# Revit family: 6_天吊埋込タイプ 消音形 単相100V_3相200V-60
name_source: partatom
category: 機械設備
units: mm (PartAtom-declared; Revit-internal decimal feet)

## family parameters
OmniClass タイトル = Centrifugal Fans
OmniClass 番号 = 23.75.35.17.27
パーツ タイプ = 割り込み
ロード時にボイドで切り取り = いいえ
丸型コネクタ寸法 = 直径を使用
作業面ベース = いいえ
共有 = いいえ
常に垂直 = はい
部屋計算ポイント = はい

## types (18) — shared parameters
Clearance Left = 450  [stored 1.47638 ft]
IfcExportAs = IfcFanType
IfcExportType = CENTRIFUGALFORWARDCURVED
MID静圧 = 0.0 Pa
MID風量 = 0.0 m³/h
OmniClassCode = 23-33 31 19 13 15
URL = https://www.mitsubishielectric.co.jp
Uniclass2015Code = Pr_65_67_29_12
Uniclass2015Title = Centrifugal fans
Uniclass2015Version = Systems v1.9
サービススペース = はい
ファンの種類 = 多翼形
仕様書バージョン = Version1.0
企業コード = 108420
分類コード = 50052502100020
参照している仕様書等のバージョン = 公共建築工事標準仕様書（機械設備工事編）平成31年度版
周波数 = 60 Hz
呼称 = 消音ボックス付送風機
本体マテリアル = 溶融亜鉛めっき鋼板
極 = 4
法定耐用年数 = 15
盤工事区分 = 電気工事
積算_科目 = 2 換気設備
製品出荷対象 = 国内
製造元 = 三菱電機株式会社
設置方法 = 天吊
説明 = ストレートシロッコファン天吊埋込タイプ（消音形）
負荷分類 = 3_ファン類
運転質量 = 0.00 kg
zero-valued in all types: Clearance Back, Clearance Bottom, Clearance Front, Clearance Right, Clearance Top

## per-type parameters (varying)
- BFS-15SUG: Depth=360  [stored 1.1811 ft]; Height=225  [stored 0.738189 ft]; M=60  [stored 0.19685 ft]; MAX静圧=62.0 Pa; MAX風量=150.0 m³/h; MIN静圧=25.0 Pa; MIN風量=96.0 m³/h; Width=273  [stored 0.895669 ft]; ダクト径=100 mm; 価格=43500 $; 天吊金具ピッチ奥行=325  [stored 1.06627 ft]; 天吊金具ピッチ幅=349  [stored 1.14501 ft]; 形名=BFS-SUG : BFS-15SUG; 極数=2; 消費電力=24 W; 番手=#1; 相=1; 製品リリース年月=2018年4月23日; 製品質量=7.00 kg; 質量=8.40 kg; 電動機出力=8 W; 電圧=100 V; 騒音レベル(dB(A))=33; 騒音レベル(dB(A))_側面=19; 騒音レベル(dB(A))_吐出=33; 騒音レベル(dB(A))_吸込=22
- BFS-30SUG: Depth=428  [stored 1.4042 ft]; Height=225  [stored 0.738189 ft]; M=70  [stored 0.229659 ft]; MAX静圧=39.0 Pa; MAX風量=300.0 m³/h; MIN静圧=15.0 Pa; MIN風量=182.0 m³/h; Width=273  [stored 0.895669 ft]; ダクト径=150 mm; 価格=60500 $; 天吊金具ピッチ奥行=393  [stored 1.28937 ft]; 天吊金具ピッチ幅=349  [stored 1.14501 ft]; 形名=BFS-SUG : BFS-30SUG; 極数=2; 消費電力=45 W; 番手=#1; 相=1; 製品リリース年月=2018年4月23日; 製品質量=7.50 kg; 質量=9.00 kg; 電動機出力=16 W; 電圧=100 V; 騒音レベル(dB(A))=40; 騒音レベル(dB(A))_側面=19.5; 騒音レベル(dB(A))_吐出=40; 騒音レベル(dB(A))_吸込=26.5
- BFS-40SUG: Depth=454  [stored 1.4895 ft]; Height=255  [stored 0.836614 ft]; M=70  [stored 0.229659 ft]; MAX静圧=78.0 Pa; MAX風量=400.0 m³/h; MIN静圧=37.0 Pa; MIN風量=273.0 m³/h; Width=305  [stored 1.00066 ft]; ダクト径=150 mm; 価格=72400 $; 天吊金具ピッチ奥行=419; 天吊金具ピッチ幅=381  [stored 1.25 ft]; 形名=BFS-SUG : BFS-40SUG; 極数=2; 消費電力=65 W; 番手=#1 1/4; 相=1; 製品リリース年月=2018年4月23日; 製品質量=9.50 kg; 質量=11.40 kg; 電動機出力=25 W; 電圧=100 V; 騒音レベル(dB(A))=44; 騒音レベル(dB(A))_側面=20.5; 騒音レベル(dB(A))_吐出=44; 騒音レベル(dB(A))_吸込=27
- BFS-50SUG: Depth=573  [stored 1.87992 ft]; Height=255  [stored 0.836614 ft]; M=85  [stored 0.278871 ft]; MAX静圧=157.0 Pa; MAX風量=500.0 m³/h; MIN静圧=81.0 Pa; MIN風量=360.0 m³/h; Width=375  [stored 1.23031 ft]; ダクト径=200 mm; 価格=10200 $; 天吊金具ピッチ奥行=538  [stored 1.76509 ft]; 天吊金具ピッチ幅=451  [stored 1.47966 ft]; 形名=BFS-SUG : BFS-50SUG; 極数=2; 消費電力=88 W; 番手=#1 1/4; 相=1; 製品リリース年月=2018年4月23日; 製品質量=13.00 kg; 質量=15.60 kg; 電動機出力=45 W; 電圧=100 V; 騒音レベル(dB(A))=49; 騒音レベル(dB(A))_側面=23; 騒音レベル(dB(A))_吐出=49; 騒音レベル(dB(A))_吸込=29.5
- BFS-65SUG: Depth=638  [stored 2.09318 ft]; Height=305  [stored 1.00066 ft]; M=85  [stored 0.278871 ft]; MAX静圧=157.0 Pa; MAX風量=650.0 m³/h; MIN静圧=94.0 Pa; MIN風量=501.0 m³/h; Width=423  [stored 1.3878 ft]; ダクト径=200 mm; 価格=107000 $; 天吊金具ピッチ奥行=603; 天吊金具ピッチ幅=499  [stored 1.63714 ft]; 形名=BFS-SUG : BFS-65SUG; 極数=2; 消費電力=125 W; 番手=#1 1/4; 相=1; 製品リリース年月=2018年4月23日; 製品質量=16.00 kg; 質量=19.20 kg; 電動機出力=65 W; 電圧=100 V; 騒音レベル(dB(A))=51; 騒音レベル(dB(A))_側面=24.5; 騒音レベル(dB(A))_吐出=51; 騒音レベル(dB(A))_吸込=29.5
- BFS-80SUG: Depth=638  [stored 2.09318 ft]; Height=305  [stored 1.00066 ft]; M=85  [stored 0.278871 ft]; MAX静圧=157.0 Pa; MAX風量=800.0 m³/h; MIN静圧=84.0 Pa; MIN風量=596.0 m³/h; Width=423  [stored 1.3878 ft]; ダクト径=200 mm; 価格=114000 $; 天吊金具ピッチ奥行=603; 天吊金具ピッチ幅=499  [stored 1.63714 ft]; 形名=BFS-SUG : BFS-80SUG; 極数=2; 消費電力=159 W; 番手=#1 1/4; 相=1; 製品リリース年月=2018年4月23日; 製品質量=16.50 kg; 質量=19.80 kg; 電動機出力=80 W; 電圧=100 V; 騒音レベル(dB(A))=53; 騒音レベル(dB(A))_側面=27; 騒音レベル(dB(A))_吐出=53; 騒音レベル(dB(A))_吸込=32
- BFS-90SUG: Depth=638  [stored 2.09318 ft]; Height=305  [stored 1.00066 ft]; M=85  [stored 0.278871 ft]; MAX静圧=206.0 Pa; MAX風量=900.0 m³/h; MIN静圧=116.0 Pa; MIN風量=676.0 m³/h; Width=443  [stored 1.45341 ft]; ダクト径=200 mm; 価格=119000 $; 天吊金具ピッチ奥行=603; 天吊金具ピッチ幅=519; 形名=BFS-SUG : BFS-90SUG; 極数=2; 消費電力=202 W; 番手=#1 1/2; 相=1; 製品リリース年月=2018年4月23日; 製品質量=18.50 kg; 質量=22.20 kg; 電動機出力=110 W; 電圧=100 V; 騒音レベル(dB(A))=55; 騒音レベル(dB(A))_側面=29; 騒音レベル(dB(A))_吐出=55; 騒音レベル(dB(A))_吸込=34.5
- BFS-100SUG: Depth=638  [stored 2.09318 ft]; Height=305  [stored 1.00066 ft]; M=85  [stored 0.278871 ft]; MAX静圧=255.0 Pa; MAX風量=1000.0 m³/h; MIN静圧=189.0 Pa; MIN風量=861.0 m³/h; Width=443  [stored 1.45341 ft]; ダクト径=200 mm; 価格=128000 $; 天吊金具ピッチ奥行=603; 天吊金具ピッチ幅=519; 形名=BFS-SUG : BFS-100SUG; 極数=2; 消費電力=247 W; 番手=#1 1/2; 相=1; 製品リリース年月=2018年4月23日; 製品質量=19.00 kg; 質量=22.80 kg; 電動機出力=160 W; 電圧=100 V; 騒音レベル(dB(A))=58; 騒音レベル(dB(A))_側面=31.5; 騒音レベル(dB(A))_吐出=58; 騒音レベル(dB(A))_吸込=37
- BFS-120SUG: Depth=668; Height=350  [stored 1.14829 ft]; M=85  [stored 0.278871 ft]; MAX静圧=265.0 Pa; MAX風量=1200.0 m³/h; MIN静圧=179.0 Pa; MIN風量=989.0 m³/h; Width=455; ダクト径=250 mm; 価格=140800 $; 天吊金具ピッチ奥行=633  [stored 2.07677 ft]; 天吊金具ピッチ幅=531  [stored 1.74213 ft]; 形名=BFS-SUG : BFS-120SUG; 極数=2; 消費電力=348 W; 番手=#1 1/2; 相=1; 製品リリース年月=2018年4月23日; 製品質量=22.00 kg; 質量=26.40 kg; 電動機出力=200 W; 電圧=100 V; 騒音レベル(dB(A))=58; 騒音レベル(dB(A))_側面=32.5; 騒音レベル(dB(A))_吐出=58; 騒音レベル(dB(A))_吸込=41
- BFS-150SUG: Depth=768; Height=350  [stored 1.14829 ft]; M=85  [stored 0.278871 ft]; MAX静圧=294.0 Pa; MAX風量=1500.0 m³/h; MIN静圧=179.0 Pa; MIN風量=1164.0 m³/h; Width=455; ダクト径=250 mm; 価格=146300 $; 天吊金具ピッチ奥行=733; 天吊金具ピッチ幅=531  [stored 1.74213 ft]; 形名=BFS-SUG : BFS-150SUG; 極数=2; 消費電力=484 W; 番手=#1 1/2; 相=1; 製品リリース年月=2018年4月23日; 製品質量=24.00 kg; 質量=28.80 kg; 電動機出力=340 W; 電圧=100 V; 騒音レベル(dB(A))=63; 騒音レベル(dB(A))_側面=34; 騒音レベル(dB(A))_吐出=63; 騒音レベル(dB(A))_吸込=42.5
- BFS-80TUG: Depth=638  [stored 2.09318 ft]; Height=305  [stored 1.00066 ft]; M=85  [stored 0.278871 ft]; MAX静圧=157.0 Pa; MAX風量=800.0 m³/h; MIN静圧=72.0 Pa; MIN風量=542.0 m³/h; Width=423  [stored 1.3878 ft]; ダクト径=200 mm; 価格=114000 $; 天吊金具ピッチ奥行=603; 天吊金具ピッチ幅=499  [stored 1.63714 ft]; 形名=BFS-TUG : BFS-80TUG; 極数=3; 消費電力=152 W; 番手=#1 1/4; 相=3; 製品リリース年月=2018年4月23日; 製品質量=18.00 kg; 質量=21.60 kg; 電動機出力=80 W; 電圧=200 V; 騒音レベル(dB(A))=53; 騒音レベル(dB(A))_側面=26.5; 騒音レベル(dB(A))_吐出=53; 騒音レベル(dB(A))_吸込=32.5
- BFS-90TUG: Depth=638  [stored 2.09318 ft]; Height=305  [stored 1.00066 ft]; M=85  [stored 0.278871 ft]; MAX静圧=206.0 Pa; MAX風量=900.0 m³/h; MIN静圧=95.0 Pa; MIN風量=612.0 m³/h; Width=443  [stored 1.45341 ft]; ダクト径=200 mm; 価格=119000 $; 天吊金具ピッチ奥行=603; 天吊金具ピッチ幅=519; 形名=BFS-TUG : BFS-90TUG; 極数=3; 消費電力=187 W; 番手=#1 1/2; 相=3; 製品リリース年月=2018年4月23日; 製品質量=18.00 kg; 質量=21.60 kg; 電動機出力=100 W; 電圧=200 V; 騒音レベル(dB(A))=55; 騒音レベル(dB(A))_側面=29; 騒音レベル(dB(A))_吐出=55; 騒音レベル(dB(A))_吸込=34.5
- BFS-100TUG: Depth=638  [stored 2.09318 ft]; Height=305  [stored 1.00066 ft]; M=85  [stored 0.278871 ft]; MAX静圧=255.0 Pa; MAX風量=1000.0 m³/h; MIN静圧=124.0 Pa; MIN風量=694.0 m³/h; Width=443  [stored 1.45341 ft]; ダクト径=200 mm; 価格=128000 $; 天吊金具ピッチ奥行=603; 天吊金具ピッチ幅=519; 形名=BFS-TUG : BFS-100TUG; 極数=3; 消費電力=230 W; 番手=#1 1/2; 相=3; 製品リリース年月=2018年4月23日; 製品質量=18.50 kg; 質量=22.20 kg; 電動機出力=150 W; 電圧=200 V; 騒音レベル(dB(A))=58; 騒音レベル(dB(A))_側面=31; 騒音レベル(dB(A))_吐出=58; 騒音レベル(dB(A))_吸込=37
- BFS-120TUG: Depth=668; Height=350  [stored 1.14829 ft]; M=85  [stored 0.278871 ft]; MAX静圧=265.0 Pa; MAX風量=1200.0 m³/h; MIN静圧=119.0 Pa; MIN風量=789.0 m³/h; Width=455; ダクト径=250 mm; 価格=140800 $; 天吊金具ピッチ奥行=633  [stored 2.07677 ft]; 天吊金具ピッチ幅=531  [stored 1.74213 ft]; 形名=BFS-TUG : BFS-120TUG; 極数=3; 消費電力=319 W; 番手=#1 1/2; 相=3; 製品リリース年月=2018年4月23日; 製品質量=22.00 kg; 質量=26.40 kg; 電動機出力=180 W; 電圧=200 V; 騒音レベル(dB(A))=58; 騒音レベル(dB(A))_側面=32.5; 騒音レベル(dB(A))_吐出=58; 騒音レベル(dB(A))_吸込=41
- BFS-150TUG: Depth=768; Height=350  [stored 1.14829 ft]; M=85  [stored 0.278871 ft]; MAX静圧=294.0 Pa; MAX風量=1500.0 m³/h; MIN静圧=142.0 Pa; MIN風量=1046.0 m³/h; Width=455; ダクト径=250 mm; 価格=146300 $; 天吊金具ピッチ奥行=733; 天吊金具ピッチ幅=531  [stored 1.74213 ft]; 形名=BFS-TUG : BFS-150TUG; 極数=3; 消費電力=445 W; 番手=#1 1/2; 相=3; 製品リリース年月=2018年4月23日; 製品質量=24.00 kg; 質量=28.80 kg; 電動機出力=280 W; 電圧=200 V; 騒音レベル(dB(A))=63; 騒音レベル(dB(A))_側面=34; 騒音レベル(dB(A))_吐出=63; 騒音レベル(dB(A))_吸込=42.5
- BFS-180TUG: Depth=768; Height=350  [stored 1.14829 ft]; M=85  [stored 0.278871 ft]; MAX静圧=314.0 Pa; MAX風量=1800.0 m³/h; MIN静圧=0.0 Pa; MIN風量=0.0 m³/h; Width=505  [stored 1.65682 ft]; ダクト径=250 mm; 価格=171600 $; 天吊金具ピッチ奥行=733; 天吊金具ピッチ幅=581  [stored 1.90617 ft]; 形名=BFS-TUG : BFS-180TUG; 極数=3; 消費電力=570 W; 番手=#1 1/2; 相=3; 製品リリース年月=2018年4月23日; 製品質量=26.00 kg; 質量=31.20 kg; 電動機出力=350 W; 電圧=200 V; 騒音レベル(dB(A))=64; 騒音レベル(dB(A))_側面=34; 騒音レベル(dB(A))_吐出=64; 騒音レベル(dB(A))_吸込=43.5
- BFS-210TUG: Depth=878; Height=350  [stored 1.14829 ft]; M=100  [stored 0.328084 ft]; MAX静圧=322.0 Pa; MAX風量=2100.0 m³/h; MIN静圧=0.0 Pa; MIN風量=0.0 m³/h; Width=551  [stored 1.80774 ft]; ダクト径=300 mm; 価格=225500 $; 天吊金具ピッチ奥行=843; 天吊金具ピッチ幅=627  [stored 2.05709 ft]; 形名=BFS-TUG : BFS-210TUG; 極数=3; 消費電力=696 W; 番手=#1 1/2; 相=3; 製品リリース年月=2018年4月23日; 製品質量=29.00 kg; 質量=34.80 kg; 電動機出力=490 W; 電圧=200 V; 騒音レベル(dB(A))=67; 騒音レベル(dB(A))_側面=34.5; 騒音レベル(dB(A))_吐出=67; 騒音レベル(dB(A))_吸込=45
- BFS-240TUA: Depth=917; Height=373  [stored 1.22375 ft]; M=99  [stored 0.324803 ft]; MAX静圧=380.0 Pa; MAX風量=2400.0 m³/h; MIN静圧=0.0 Pa; MIN風量=0.0 m³/h; Width=493  [stored 1.61745 ft]; ダクト径=300 mm; 価格=221000 $; 天吊金具ピッチ奥行=864; 天吊金具ピッチ幅=602  [stored 1.97507 ft]; 形名=BFS-TUG : BFS-240TUA; 極数=3; 消費電力=810 W; 番手=#1 1/2; 相=3; 製品リリース年月=2003年4月; 製品質量=37.00 kg; 質量=44.40 kg; 電動機出力=1100 W; 電圧=200 V; 騒音レベル(dB(A))=69; 騒音レベル(dB(A))_側面=42; 騒音レベル(dB(A))_吐出=69; 騒音レベル(dB(A))_吸込=46.5

note: column(s) folded — value = type name in every type: モデル

note: [stored X ft] marks values corroborated as IEEE doubles in the binary element streams (Revit-internal decimal feet)
